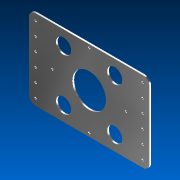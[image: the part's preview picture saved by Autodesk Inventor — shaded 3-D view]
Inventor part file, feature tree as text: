
AUTODESK INVENTOR PART (.ipt)
format: ipt  version: 2022.2 (Build 262287000, 287)  size: 159,744 bytes
history: native  units: in
note: dims shown in document units (in); Inventor stores cm internally (conversion verified against a paired STEP export)
features: sketch x1, extrude x1, hole x1
ambient origin geometry x8: Origin, YZ Plane, XZ Plane, XY Plane, X Axis, Y Axis, Z Axis, Center Point
bodies: Solid1 (feature_tree)
feature tree (3):
  sketch  "Sketch1"  dims[d1=2.7in d2=1.125in d3=2.5in d4=9.0in d5=0.5in d6=0.5in d7=1.0in d8=1.0in d10=1.0in d11=1.0in d12=1.0in d13=1.0in d14=0.5in d15=0.5in d16=0.5in d17=0.25in d18=2.7in d19=0.125in d20=0.0in d21=2.0in d22=0.17in d23=0.75in d24=0.375in d25=0.25in d26=0.5635in d27=1.0in d28=0.8108in]
  extrude  "Extrusion1"  Depth=0.125in
  hole  "Hole1"  [1 undecoded]
note: 1 required parameter value undecoded (feature->parameter linkage not recoverable at this tier; creation-order binding heuristic only, values carry confidence <= 0.55)
